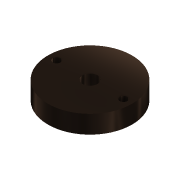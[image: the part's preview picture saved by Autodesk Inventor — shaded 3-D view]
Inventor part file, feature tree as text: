
AUTODESK INVENTOR PART (.ipt)
format: ipt  version: 2017 (Build 210142000, 142)  size: 114,688 bytes
history: native  units: mm
features: sketch x6, extrude x2, sweep x2
ambient origin geometry x8: Origin, YZ Plane, XZ Plane, XY Plane, X Axis, Y Axis, Z Axis, Center Point
bodies: Solid1 (feature_tree)
feature tree (10):
  extrude  "Extrusion1"  Depth=3.0mm TaperAngle=0.0deg
  extrude  "Extrusion2"  Depth=3.0mm TaperAngle=0.0deg
  sweep  "Sweep1"
  sweep  "Sweep2"
  sketch  "Sketch1"  dims[d0=14.0mm d1=3.0mm d2=0.0mm]
  sketch  "Sketch2"  dims[d3=2.5mm d4=3.0mm d5=0.0mm]
  sketch  "Sketch3"  dims[d6=1.25mm d7=1.25mm]
  sketch  "Sketch4"  dims[d9=0.8mm d10=0.8mm]
  sketch  "Sketch5"  dims[d12=9.9mm]
  sketch  "Sketch6"  dims[d13=1.6mm d14=0.0mm d15=0.0mm d16=1.25mm d17=9.9mm d18=1.425mm d19=1.6mm d20=0.0mm d21=0.0mm]
